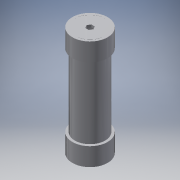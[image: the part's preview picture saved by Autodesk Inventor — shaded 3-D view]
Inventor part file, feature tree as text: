
AUTODESK INVENTOR PART (.ipt)
format: ipt  version: 2016 (Build 200138000, 138)  size: 147,456 bytes
history: native  units: in
note: dims shown in document units (in); Inventor stores cm internally (conversion verified against a paired STEP export)
features: extrude x6, sketch x6
ambient origin geometry x8: Origin, YZ Plane, XZ Plane, XY Plane, X Axis, Y Axis, Z Axis, Center Point
bodies: Body1 (feature_tree)
feature tree (12):
  extrude  "Extrusion5"  Depth=0.203in
  extrude  "Extrusion6"  Depth=7.5in
  extrude  "Extrusion7"  Depth=1.5in TaperAngle=0.0deg
  extrude  "Extrusion8"  Depth=1.5in TaperAngle=0.0deg
  extrude  "Extrusion9"  Depth=0.203in TaperAngle=0.0deg
  extrude  "Extrusion10"  Depth=9.0in TaperAngle=0.0deg
  sketch  "Sketch6"  dims[d16=2.5in d17=0.203in]
  sketch  "Sketch7"  dims[d18=7.5in d19=0.0in d20=2.5in]
  sketch  "Sketch8"  dims[d21=0.203in d22=1.5in d23=0.0in]
  sketch  "Sketch9"  dims[d24=0.203in d25=0.0in d26=1.5in d27=0.0in]
  sketch  "Sketch10"  dims[d28=2.4996in d29=0.203in d30=0.0in]
  sketch  "Sketch11"  dims[d31=0.5in d32=9.0in d33=0.0in]
